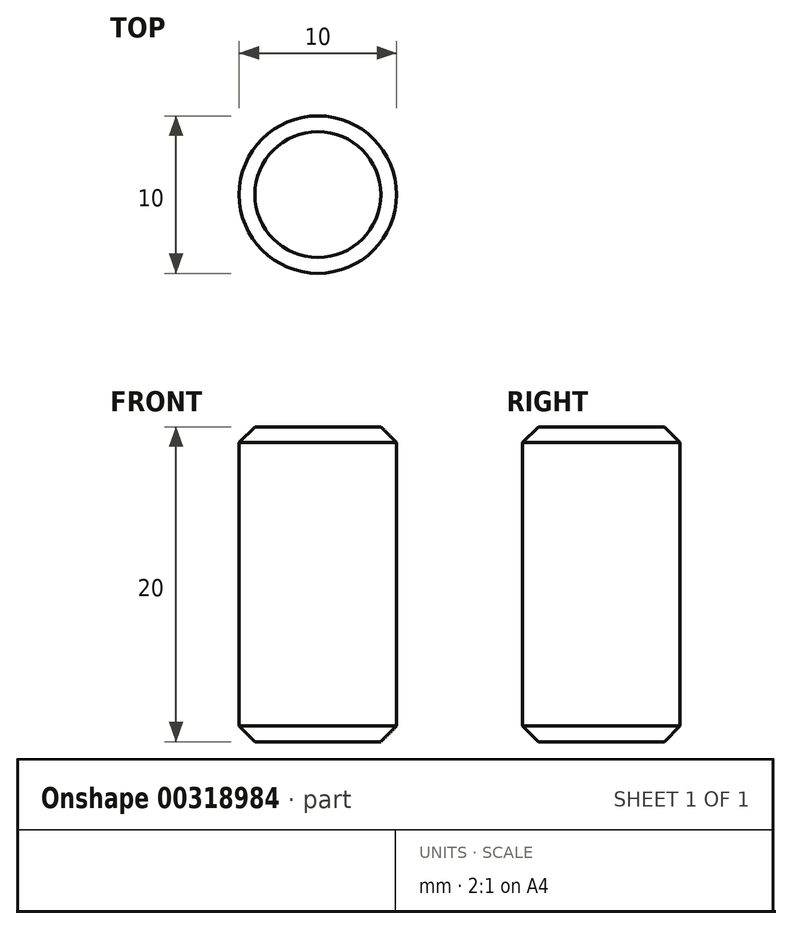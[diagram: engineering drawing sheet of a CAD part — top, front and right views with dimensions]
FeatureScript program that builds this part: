
annotation { "Feature Type Name" : "Feature", "Feature Type Description" : "" }
export const myFeature = defineFeature(function(context is Context, id is Id, definition is map)
    precondition{}
    {
        {
            var Q0;
            Q0=qCreatedBy(makeId("Top.planeOp"),FACE);
            var sketch = newSketch(context, id + "F0", { "sketchPlane" : qUnion([Q0])});
            skCircle(sketch, "E0", {"center": v(0, 0) * mm, "radius": 5 * mm});
            skSolve(sketch);
        }
        {
            var Q0;
            Q0 = qSketchRegion(id + "F0", true);
            extrude(context, id + "F1", {"entities" : qUnion([Q0]), "oppositeDirection" : true, "depth" : 20 * mm});
        }
        {
            var Q0;
            Q0=makeQuery(id+"F1.opExtrude","CAP_EDGE",EDGE,{"disambiguationData":[OSD([sQuery(id+"F0.wireOp",EDGE,"E0")])],"isStart":false});
            chamfer(context, id + "F2", {"entities" : qUnion([Q0]), "width" : 1 * mm, "tangentPropagation" : true});
        }
        {
            var Q0;
            Q0=makeQuery(id+"F1.opExtrude","CAP_FACE",FACE,{"disambiguationData":[OSD([sQuery(id+"F0.wireOp",EDGE,"E0")])],"isStart":true});
            chamfer(context, id + "F3", {"entities" : qUnion([Q0]), "width" : 1 * mm, "tangentPropagation" : true});
        }
    });
